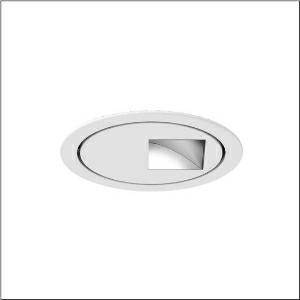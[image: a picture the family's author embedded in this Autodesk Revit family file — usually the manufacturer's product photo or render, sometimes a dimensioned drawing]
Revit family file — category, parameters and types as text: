
# Revit family: lunis_11_mini_round_51dk11b72wg21
name_source: partatom
category: Lighting Fixtures
units: mm (PartAtom-declared; Revit-internal decimal feet)

## family parameters
Cut with Voids When Loaded = No
Host = Face
Light Source = No
Part Type = Normal
Room Calculation Point = No
Round Connector Dimension = Use Diameter
Shared = No

## types (1)
- Lunis 11 mini round (1 x LED 4000K / CRI = 80 (unbekannt), 2470 lm, 4000K)
    Apparent Load = 28 VA
    CIE Flux Codes = 44 77 97 100 100
    Color Rendering = 80
    Color Temperature = 4000K
    Default Elevation = 1800 mm
    Description = Lunis 11 mini round, downlight, light control with wallwasher, of highly reflective aluminium, highly specular, light emission: direct distribution, LED rated luminous flux: 2.470lm, light colour: 840, control gear: ECG, with terminal, 3-pole, mains connection: 220..230V, AC/DC, 0/50..60Hz, LED module, luminaire module, of aluminium, highly specular, white, diameter: 176mm, clamping range: 1..40mm, recessing ring, of plastic, traffic white (RAL 9016), protection rating (complete): IP20, insulation class (complete): insulation class II (safety insulation), certification: CE, permissible ambient temperature for indoor applications: 0..+35°C, packaging unit: 1 piece
    Height = 0 mm  [stored 0 ft]
    Lamp = 1 x LED 4000K / CRI >= 80 (unbekannt)
    Lamp Light Flux = 2470 lm
    Lamp count = 1
    Length = 176 mm
    Luminous efficacy = 88 lm/W
    Manufacturer = Siteco
    ModVariant = No
    Model = 51DK11B72WG21
    Mounting Place = Ceiling
    Mounting Type = Recessed
    Number of Poles = 1
    OnlyDefault = Yes
    Power Factor = 1
    Product Name = Lunis 11 mini round
    Product group = downlight
    ProductGroupID = 400
    Protection Class = Protection class II
    Protection Degree = IP 20
    RLX_Detail_Level = 1
    RLX_Emergency_Light_Flux = 0 lm
    RLX_Emergency_Type = 0
    RLX_Emergency_Type_DB = No
    RlxData = <blob elided: 59477 chars, md5=f45e82f7>
    Socket = socket
    Standby Power = 0 W
    System Light Flux = 2470 lm
    System Power = 28 W
    Type Comments = Product without accessories
    Type Image = l_1004772.jpg
    URL = http://relux.com
    VarID = ---
    Voltage = 0 V
    Weight = 0.00 kg
    Width = 176 mm

note: [stored X ft] marks values corroborated as IEEE doubles in the binary element streams (Revit-internal decimal feet)

## geometry (parser evidence)
native form markers: Blend x4, Sweep x11
no freeform markers — native parametric forms only
